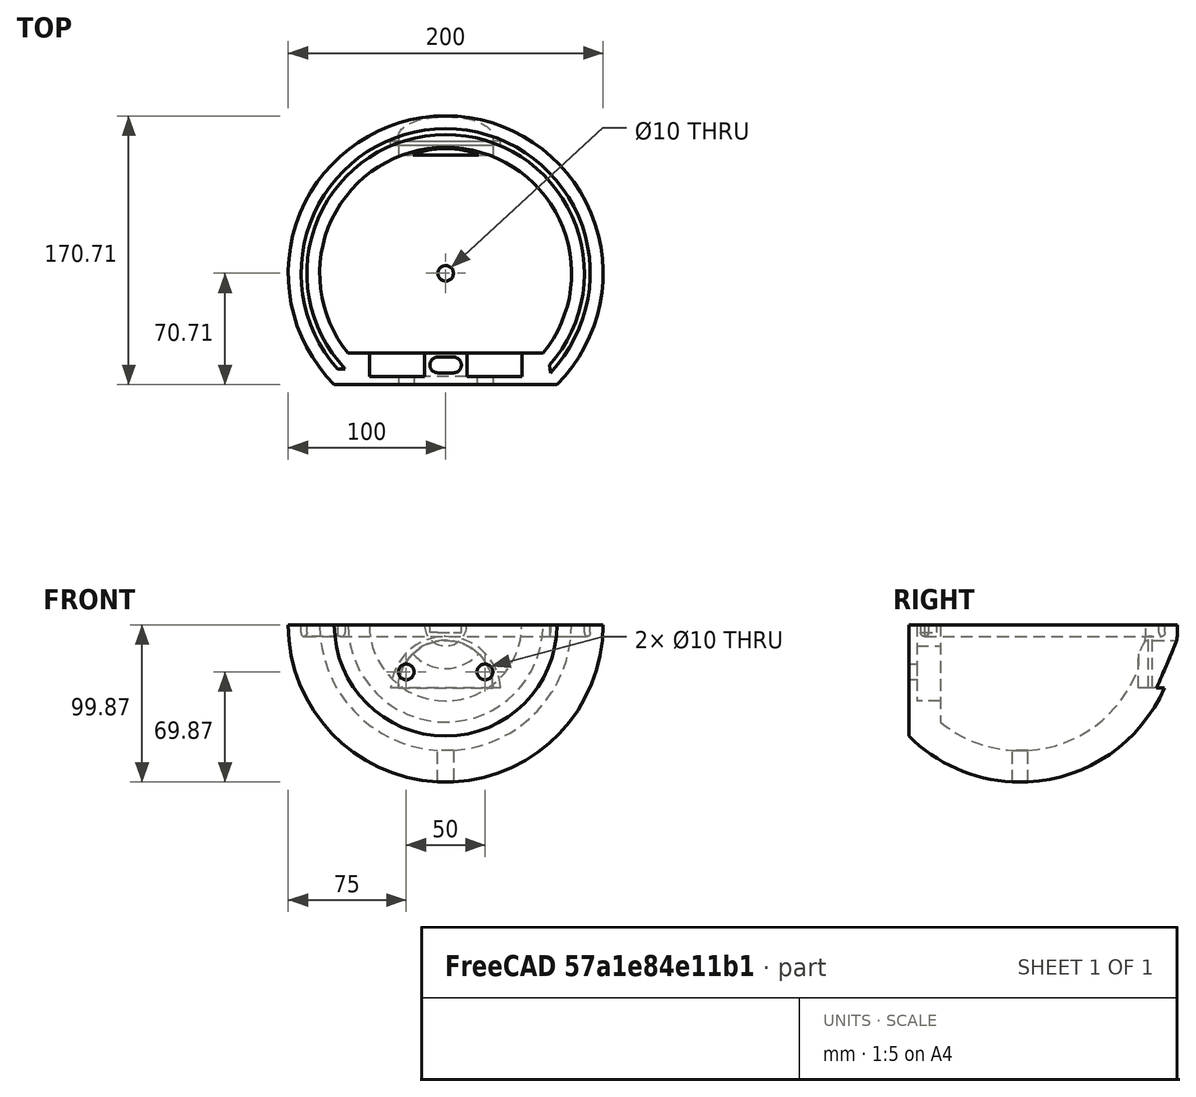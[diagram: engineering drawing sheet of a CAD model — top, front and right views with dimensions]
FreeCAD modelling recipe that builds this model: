
FCSTD DOCUMENT  (FreeCAD 0.18R4 (GitTag))
Label: Ariel Top
License: All rights reserved
LicenseURL: http://en.wikipedia.org/wiki/All_rights_reserved
objects: Sketcher::SketchObject×8, PartDesign::Pocket×5, Part::Plane×4, PartDesign::Revolution×1, PartDesign::SubtractivePipe×1, PartDesign::Mirrored×1, PartDesign::Body×1, Mesh::Feature×1
note: 28 computed .brp shape members not serialized (recipe doc carries the construction recipe); baked Part::Feature solids carry a one-line shape summary decoded from their .brp

FEATURE [Sketcher::SketchObject] Sketch
  sketch-geometry (16):
    g0: ArcOfCircle CenterX=0 CenterY=0 CenterZ=0 NormalX=0 NormalY=0 NormalZ=1 AngleXU=0 Radius=100 StartAngle=5.49779 EndAngle=7.85398
    g1: LineSegment StartX=3.06e-14 StartY=100 StartZ=0 EndX=2.43e-14 EndY=80 EndZ=0
    g2: LineSegment [constr] StartX=0 StartY=0 StartZ=0 EndX=106.066 EndY=-106.066 EndZ=0
    g3: LineSegment StartX=70.7107 StartY=-70.7107 StartZ=0 EndX=0 EndY=-70.7107 EndZ=0
    g4: LineSegment StartX=61.8743 StartY=-50.7107 StartZ=0 EndX=48.4371 EndY=-50.7107 EndZ=0
    g5: LineSegment StartX=48.4371 StartY=-50.7107 StartZ=0 EndX=48.4371 EndY=-65.7107 EndZ=0
    g6: LineSegment StartX=48.4371 StartY=-65.7107 StartZ=0 EndX=13.4371 EndY=-65.7107 EndZ=0
    g7: LineSegment StartX=13.4371 StartY=-65.7107 StartZ=0 EndX=13.4371 EndY=-50.7107 EndZ=0
    g8: LineSegment StartX=13.4371 StartY=-50.7107 StartZ=0 EndX=0 EndY=-50.7107 EndZ=0
    g9: LineSegment StartX=0 StartY=-50.7107 StartZ=0 EndX=0 EndY=-70.7107 EndZ=0
    g10: ArcOfCircle CenterX=-2e-16 CenterY=-8.2e-15 CenterZ=0 NormalX=0 NormalY=0 NormalZ=1 AngleXU=0 Radius=80 StartAngle=5.59662 EndAngle=7.85398
    g11: LineSegment [constr] StartX=0 StartY=0 StartZ=0 EndX=106.066 EndY=106.066 EndZ=0
    g12: GeomPoint X=56.5685 Y=56.5685 Z=0
    g13: GeomPoint X=70.7107 Y=70.7107 Z=0
    g14: GeomPoint X=100 Y=0 Z=0
    g15: GeomPoint X=80 Y=0 Z=0
  constraints (44):
    c: Coincident(g0,g-1)
    c: PointOnObject(g0,g-2)
    c: Radius(g0) = 100
    c: PointOnObject(g1,g-2)
    c: DistanceY(g1,g0) = 20
    c: Coincident(g1,g0)
    c: Coincident(g2,g0)
    c: Angle(g2,g-1) = 0.785398
    c: Distance(g2) = 150
    c: PointOnObject(g0,g2)
    c: Coincident(g3,g0)
    c: PointOnObject(g3,g-2)
    c: Horizontal(g3)
    c: Horizontal(g4)
    c: Coincident(g5,g4)
    c: Vertical(g5)
    c: Coincident(g6,g5)
    c: Horizontal(g6)
    c: Coincident(g7,g6)
    c: Vertical(g7)
    c: Coincident(g8,g7)
    c: PointOnObject(g8,g-2)
    c: Coincident(g9,g8)
    c: Coincident(g9,g3)
    c: DistanceX(g6,g6) = 35
    c: Horizontal(g8,g4)
    c: Horizontal(g8)
    c: DistanceY(g3,g6) = 5
    c: Equal(g1,g9)
    c: Coincident(g10,g1)
    c: Coincident(g10,g4)
    c: Coincident(g11,g0)
    c: Symmetric(g11,g2,g-1)
    c: PointOnObject(g12,g10)
    c: PointOnObject(g13,g0)
    c: PointOnObject(g12,g11)
    c: PointOnObject(g13,g11)
    c: Distance(g13,g12) = 20
    c: PointOnObject(g14,g0)
    c: PointOnObject(g15,g10)
    c: PointOnObject(g15,g-1)
    c: PointOnObject(g14,g-1)
    c: Distance(g15,g14) = 20
    c: Equal(g4,g8)
FEATURE [PartDesign::Revolution] Revolution
  Angle = 180
  Axis = (0,1,0)
  Base = (0,0,0)
  Profile = -> Sketch
  ReferenceAxis = -> Sketch [V_Axis]
FEATURE [Sketcher::SketchObject] Sketch001
  ExternalGeometry = -> [Revolution]
  MapMode = 5
  Support = -> [XY_Plane]
  sketch-geometry (6):
    g0: LineSegment [constr] StartX=-61.8743 StartY=-50.7107 StartZ=0 EndX=-70.7107 EndY=-70.7107 EndZ=0
    g1: LineSegment [constr] StartX=61.8743 StartY=-50.7107 StartZ=0 EndX=70.7107 EndY=-70.7107 EndZ=0
    g2: GeomPoint X=-66.2925 Y=-60.7108 Z=0
    g3: GeomPoint X=66.2925 Y=-60.7108 Z=0
    g4: GeomPoint X=0 Y=90 Z=0
    g5: ArcOfCircle CenterX=-7.8e-15 CenterY=0.0646747 CenterZ=0 NormalX=0 NormalY=0 NormalZ=1 AngleXU=0 Radius=89.9353 StartAngle=5.54118 EndAngle=10.1668
  constraints (13):
    c: Coincident(g0,g-8)
    c: Coincident(g0,g-12)
    c: Coincident(g1,g-7)
    c: Coincident(g1,g-11)
    c: PointOnObject(g2,g0)
    c: PointOnObject(g3,g1)
    c: Distance(g2,g0) = 10.9327
    c: PointOnObject(g4,g-2)
    c: Horizontal(g3,g2)
    c: DistanceY(g4,g-10) = 10
    c: Coincident(g5,g2)
    c: Coincident(g5,g3)
    c: PointOnObject(g4,g5)
FEATURE [Part::Plane] Plane
  AttacherType = Attacher::AttachEngine3D
  Length = 10
  Placement = pos=(0,-60.711,0) rot=(0.57735,0.57735,0.57735;4.18879rad)
  Width = 10
FEATURE [Sketcher::SketchObject] Sketch002
  ExternalGeometry = -> [Revolution]
  MapMode = 5
  Placement = pos=(0,-60.711,0) rot=(0.57735,0.57735,0.57735;4.18879rad)
  Support = -> [Plane]
  sketch-geometry (5):
    g0: ArcOfCircle CenterX=5 CenterY=-66.2925 CenterZ=0 NormalX=0 NormalY=0 NormalZ=1 AngleXU=0 Radius=2.5 StartAngle=4.71239 EndAngle=7.85398
    g1: ArcOfCircle CenterX=-5 CenterY=-66.2925 CenterZ=0 NormalX=0 NormalY=0 NormalZ=1 AngleXU=0 Radius=2.5 StartAngle=1.5708 EndAngle=4.71239
    g2: LineSegment StartX=5 StartY=-63.7925 StartZ=0 EndX=-5 EndY=-63.7925 EndZ=0
    g3: LineSegment StartX=5 StartY=-68.7925 StartZ=0 EndX=-5 EndY=-68.7925 EndZ=0
    g4: GeomPoint X=0 Y=-63.7925 Z=0
  constraints (12):
    c: Tangent(g0,g3) = 1.5708
    c: Tangent(g0,g2) = -1.5708
    c: Tangent(g2,g1) = -1.5708
    c: Tangent(g3,g1) = 1.5708
    c: Horizontal(g2)
    c: Equal(g0,g1)
    c: Radius(g0) = 2.5
    c: DistanceX(g2,g2) = 10
    c: Symmetric(g0,g1,g4)
    c: PointOnObject(g4,g-2)
    c: DistanceY(g-4,g-3) = 8.83639
    c: DistanceY(g0,g-3) = 4.41819
FEATURE [PartDesign::SubtractivePipe] SubtractivePipe
  AuxilleryCurvelinear = true
  AuxillerySpineTangent = false
  BaseFeature = -> Revolution
  Binormal = (0,0,0)
  Mode = 0
  Profile = -> Sketch002
  Spine = -> Sketch001
  SpineTangent = false
  Transformation = 0
  Transition = 0
FEATURE [Sketcher::SketchObject] Sketch003
  ExternalGeometry = -> [SubtractivePipe]
  MapMode = 5
  Support = -> [XY_Plane]
  sketch-geometry (4):
    g0: ArcOfCircle CenterX=-5 CenterY=-58.2107 CenterZ=0 NormalX=0 NormalY=0 NormalZ=1 AngleXU=0 Radius=5 StartAngle=1.5708 EndAngle=4.71239
    g1: ArcOfCircle CenterX=5 CenterY=-58.2107 CenterZ=0 NormalX=0 NormalY=0 NormalZ=1 AngleXU=0 Radius=5 StartAngle=4.71239 EndAngle=7.85398
    g2: LineSegment StartX=-5 StartY=-63.2107 StartZ=0 EndX=5 EndY=-63.2107 EndZ=0
    g3: LineSegment StartX=-5 StartY=-53.2107 StartZ=0 EndX=5 EndY=-53.2107 EndZ=0
  constraints (10):
    c: Tangent(g0,g3) = 1.5708
    c: Tangent(g0,g2) = -1.5708
    c: Tangent(g2,g1) = -1.5708
    c: Tangent(g3,g1) = 1.5708
    c: Horizontal(g2)
    c: Radius(g1) = 5
    c: Symmetric(g0,g1,g-2)
    c: DistanceX(g3,g3) = 10
    c: DistanceY(g-9,g-4) = 15
    c: DistanceY(g0,g-4) = 7.5
FEATURE [PartDesign::Pocket] Pocket
  BaseFeature = -> SubtractivePipe
  Length = 5
  Length2 = 100
  Profile = -> Sketch003
  Type = 0
FEATURE [Sketcher::SketchObject] Sketch004
  MapMode = 5
  Support = -> [XY_Plane]
  sketch-geometry (1):
    g0: Circle CenterX=0 CenterY=0 CenterZ=0 NormalX=0 NormalY=0 NormalZ=1 AngleXU=0 Radius=5
  constraints (2):
    c: Coincident(g0,g-1)
    c: Radius(g0) = 5
FEATURE [PartDesign::Pocket] Pocket001
  BaseFeature = -> Pocket
  Length = 5
  Length2 = 100
  Profile = -> Sketch004
  Type = 1
FEATURE [Part::Plane] Plane001
  AttacherType = Attacher::AttachEngine3D
  Length = 10
  Placement = pos=(0,100,0) rot=(0.57735,0.57735,0.57735;4.18879rad)
  Width = 10
FEATURE [Sketcher::SketchObject] Sketch005
  MapMode = 5
  Placement = pos=(0,100,0) rot=(0.57735,0.57735,0.57735;4.18879rad)
  Support = -> [Plane001]
  sketch-geometry (2):
    g0: ArcOfCircle CenterX=-40 CenterY=0 CenterZ=0 NormalX=0 NormalY=0 NormalZ=1 AngleXU=0 Radius=30 StartAngle=4.71239 EndAngle=7.85398
    g1: LineSegment StartX=-40 StartY=30 StartZ=0 EndX=-40 EndY=-30 EndZ=0
  constraints (7):
    c: Vertical(g0,g0)
    c: Radius(g0) = 30
    c: PointOnObject(g0,g-1)
    c: DistanceX(g0,g-1) = 40
    c: Coincident(g1,g0)
    c: Coincident(g1,g0)
    c: DistanceY(g1,g1) = 60
FEATURE [PartDesign::Pocket] Pocket002
  BaseFeature = -> Pocket001
  Length = 25
  Length2 = 100
  Profile = -> Sketch005
  Type = 0
FEATURE [Part::Plane] Plane002
  AttacherType = Attacher::AttachEngine3D
  Length = 10
  Placement = pos=(0,81.5,0) rot=(0.57735,0.57735,0.57735;4.18879rad)
  Width = 10
FEATURE [Sketcher::SketchObject] Sketch006
  ExternalGeometry = -> [Sketch005]
  MapMode = 5
  Placement = pos=(0,81.5,0) rot=(0.57735,0.57735,0.57735;4.18879rad)
  Support = -> [Plane002]
  sketch-geometry (4):
    g0: ArcOfCircle CenterX=-42.5 CenterY=0 CenterZ=0 NormalX=0 NormalY=0 NormalZ=1 AngleXU=0 Radius=35 StartAngle=4.78388 EndAngle=7.78249
    g1: LineSegment StartX=-40 StartY=34.9106 StartZ=0 EndX=-40 EndY=-34.9106 EndZ=0
    g2: GeomPoint X=-10 Y=0 Z=0
    g3: GeomPoint X=-7.5 Y=0 Z=0
  constraints (11):
    c: PointOnObject(g0,g-1)
    c: Vertical(g0,g0)
    c: Coincident(g1,g0)
    c: Coincident(g1,g0)
    c: DistanceX(g0,g-1) = 42.5
    c: PointOnObject(g2,g-1)
    c: PointOnObject(g3,g-1)
    c: PointOnObject(g3,g0)
    c: PointOnObject(g2,g-4)
    c: DistanceX(g2,g3) = 2.5
    c: Vertical(g0,g-4)
FEATURE [PartDesign::Pocket] Pocket003
  BaseFeature = -> Pocket002
  Length = 2.5
  Length2 = 100
  Profile = -> Sketch006
  Reversed = true
  Type = 0
FEATURE [Part::Plane] Plane003
  AttacherType = Attacher::AttachEngine3D
  Length = 10
  Placement = pos=(0,-75,0) rot=(0.57735,0.57735,0.57735;4.18879rad)
  Width = 10
FEATURE [Sketcher::SketchObject] Sketch007
  MapMode = 5
  Placement = pos=(0,-75,0) rot=(0.57735,0.57735,0.57735;4.18879rad)
  Support = -> [Plane003]
  sketch-geometry (1):
    g0: Circle CenterX=-30 CenterY=25 CenterZ=0 NormalX=0 NormalY=0 NormalZ=1 AngleXU=0 Radius=5
  constraints (3):
    c: Radius(g0) = 5
    c: DistanceY(g-1,g0) = 25
    c: DistanceX(g0,g-1) = 30
FEATURE [PartDesign::Pocket] Pocket004
  BaseFeature = -> Pocket003
  Length = 10
  Length2 = 100
  Profile = -> Sketch007
  Reversed = true
  Type = 0
FEATURE [PartDesign::Mirrored] Mirrored
  BaseFeature = -> Pocket004
  MirrorPlane = -> YZ_Plane
  Originals = -> [Pocket004]
FEATURE [PartDesign::Body] Body
  Group = -> [Sketch,Revolution,Sketch001,Sketch002,SubtractivePipe,Sketch003,Pocket,Sketch004,Pocket001,Sketch005,Pocket002,Sketch006,Pocket003,Sketch007,Pocket004,Mirrored]
  Origin = -> Origin
  Tip = -> Mirrored
FEATURE [Mesh::Feature] Mesh  label="Body (Meshed)"
